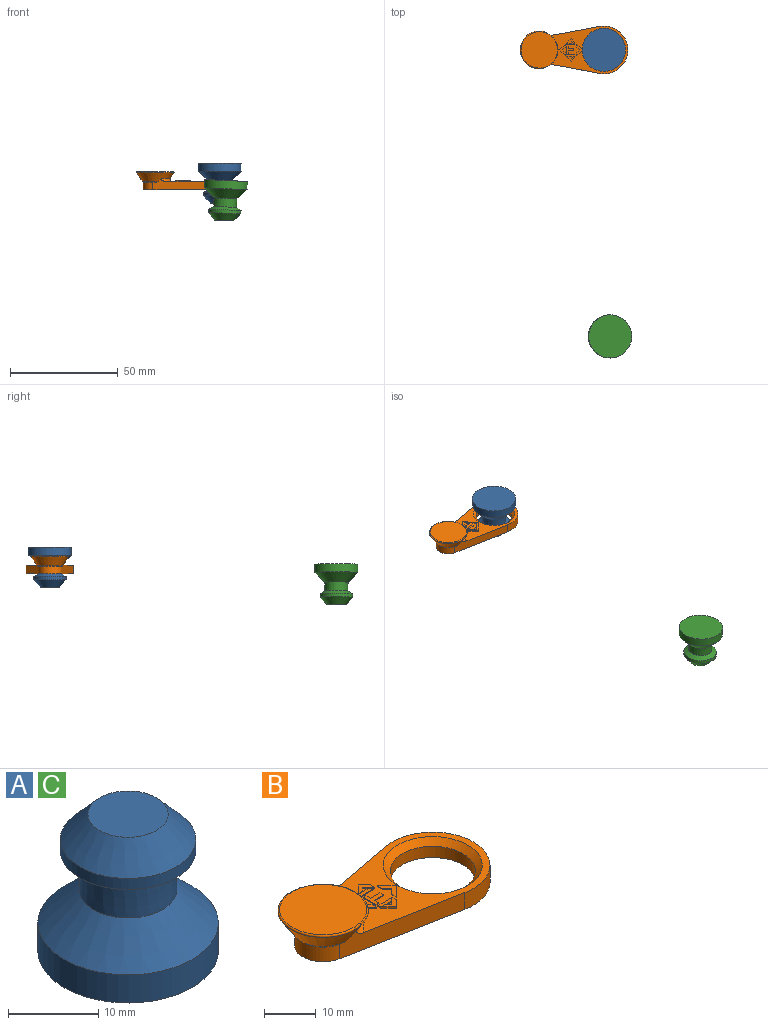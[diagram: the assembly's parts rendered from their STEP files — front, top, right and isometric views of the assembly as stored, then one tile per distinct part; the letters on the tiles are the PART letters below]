
ASSEMBLY  parts=3 mates=1
PART A: 8 faces, bbox 20x20x18.6 mm
  f0: cylinder r=7.51mm len=15.03mm, axis (0,0,1), area 71.2mm2, adj f1,f7
  f1: cone r=7.51mm half-angle=57.5deg, axis (0,0,1), area 104.1mm2, adj f0,f2
  f2: cone r=5.34mm half-angle=0.8deg, axis (0,0,-1), area 133.8mm2, adj f1,f3
  f3: cone r=10mm half-angle=45.9deg, axis (0,0,-1), area 310.4mm2, adj f2,f4
  f4: cylinder r=10mm len=20mm, axis (0,0,1), area 239.6mm2, adj f3,f5
  f5: plane 20x20mm, normal (0,0,-1), area 314.2mm2, adj f4
  f6: plane 8.89x8.89mm, normal (0,0,1), area 62.1mm2, adj f7
  f7: cone r=4.45mm half-angle=41.9deg, axis (0,0,-1), area 172.6mm2, adj f0,f6
PART B: 64 faces, bbox 50.6x22.2x8.5 mm
  f0: plane 36.62x22.2mm, normal (0,0,1), area 296.5mm2, adj f3,f8,f9,f10,f16,f20,f21,f23
  f1: plane 1.72x0.86mm, normal (0,0,1), area 0.7mm2, adj f32,f51,f55
  f2: plane 1.72x0.86mm, normal (0,0,1), area 0.7mm2, adj f19,f45,f46
  f3: cone r=7.6mm half-angle=45deg, axis (0,0,1), area 107.1mm2, adj f0,f18
  f4: plane 16.88x16.88mm, normal (0,0,1), area 223.8mm2, adj f17
  f5: cone r=6mm half-angle=33.7deg, axis (0,0,1), area 197.3mm2, adj f8,f9,f13,f14,f15,f16,f17
  f6: cylinder r=5.53mm len=10.86mm, axis (0,0,-1), area 53.5mm2, adj f8,f9,f11,f14
  f7: cylinder r=4.03mm len=8.05mm, axis (0,0,-1), area 199.8mm2, adj f11,f12
  f8: plane 28.96x5.55mm, normal (-0.19,0.98,0), area 118.4mm2, adj f0,f5,f6,f10,f11,f13,f16
  f9: plane 28.96x5.55mm, normal (-0.19,-0.98,0), area 118.4mm2, adj f0,f5,f6,f10,f11,f15,f16
  f10: cylinder r=11.1mm len=22.2mm, axis (0,0,-1), area 156.1mm2, adj f0,f8,f9,f11
  f11: plane 46.63x22.2mm, normal (0,0,-1), area 484.2mm2, adj f6,f7,f8,f9,f10,f18
  f12: plane 8.05x8.05mm, normal (0,0,-1), area 50.9mm2, adj f7
  f13: plane 1.32x0.45mm, normal (-0.13,0.69,-0.71), area 0.5mm2, adj f5,f8,f14
  f14: cone r=5.53mm half-angle=45deg, axis (0,0,1), area 9.5mm2, adj f5,f6,f13,f15
  f15: plane 1.32x0.45mm, normal (-0.13,-0.69,-0.71), area 0.5mm2, adj f5,f9,f14
  f16: torus R=7.87mm, axis (0,0,1), area 33.1mm2, adj f0,f5,f8,f9
  f17: torus R=8.44mm, axis (0,0,1), area 35.2mm2, adj f4,f5
  f18: cylinder r=8.25mm len=16.5mm, axis (0,0,-1), area 137.4mm2, adj f3,f11
  f19: plane 1.72x0.2mm, normal (0,1,0), area 0.3mm2, adj f2,f22,f45,f46
  f20: plane 0.8x0.2mm, normal (-1,0,0), area 0.2mm2, adj f0,f21,f22,f44
  f21: plane 3.79x0.2mm, normal (0,-1,0), area 0.8mm2, adj f0,f20,f22,f47
  f22: plane 3.79x0.8mm, normal (0,0,1), area 2.7mm2, adj f19,f20,f21,f43,f46
  f23: plane 3.51x0.2mm, normal (-1,0,0), area 0.7mm2, adj f0,f24,f30,f31
  f24: plane 0.8x0.2mm, normal (0,-1,0), area 0.2mm2, adj f0,f23,f25,f31
  f25: plane 1.28x0.2mm, normal (1,0,0), area 0.3mm2, adj f0,f24,f26,f31
  f26: plane 2.53x0.2mm, normal (0,-1,0), area 0.5mm2, adj f0,f25,f27,f31
  f27: plane 0.94x0.2mm, normal (1,0,0), area 0.2mm2, adj f0,f26,f28,f31
  f28: plane 2.53x0.2mm, normal (0,1,0), area 0.5mm2, adj f0,f27,f29,f31
  f29: plane 1.28x0.2mm, normal (1,0,0), area 0.3mm2, adj f0,f28,f30,f31
  f30: plane 0.8x0.2mm, normal (0,1,0), area 0.2mm2, adj f0,f23,f29,f31
  f31: plane 3.51x3.33mm, normal (0,0,1), area 5.2mm2, adj f23,f24,f25,f26,f27,f28,f29,f30
  f32: plane 1.72x0.2mm, normal (0,-1,0), area 0.3mm2, adj f1,f35,f51,f55
  f33: plane 3.79x0.2mm, normal (0,1,0), area 0.8mm2, adj f0,f34,f35,f54
  f34: plane 0.8x0.2mm, normal (-1,0,0), area 0.2mm2, adj f0,f33,f35,f52
  f35: plane 3.79x0.8mm, normal (0,0,1), area 2.7mm2, adj f32,f33,f34,f50,f51
  f36: plane 2.56x2.56mm, normal (-0.71,0.71,0), area 1.1mm2, adj f0,f37,f41,f42
  f37: plane 2.56x2.56mm, normal (-0.71,-0.71,0), area 1.1mm2, adj f0,f36,f38,f42
  f38: plane 1.27x0.3mm, normal (1,0,0), area 0.4mm2, adj f0,f37,f39,f42
  f39: plane 1.28x1.28mm, normal (0.71,0.71,0), area 0.5mm2, adj f0,f38,f40,f42
  f40: plane 1.28x1.28mm, normal (0.71,-0.71,0), area 0.5mm2, adj f0,f39,f41,f42
  f41: plane 1.27x0.3mm, normal (1,0,0), area 0.4mm2, adj f0,f36,f40,f42
  f42: plane 5.11x2.56mm, normal (0,0,1), area 4.9mm2, adj f36,f37,f38,f39,f40,f41
  f43: plane 1.27x0.1mm, normal (0,-1,0), area 0.1mm2, adj f22,f44,f45,f49
  f44: plane 2.13x2.13mm, normal (-0.71,0.71,0), area 0.9mm2, adj f0,f20,f43,f48,f49
  f45: plane 0.86x0.86mm, normal (0.71,-0.71,0), area 0.4mm2, adj f2,f19,f43,f46,f49
  f46: plane 1.66x1.66mm, normal (-0.71,-0.71,0), area 0.5mm2, adj f2,f19,f22,f45,f47,f49
  f47: plane 1.27x0.3mm, normal (1,0,0), area 0.4mm2, adj f0,f21,f46,f48,f49
  f48: plane 1.66x1.66mm, normal (0.71,0.71,0), area 0.7mm2, adj f0,f44,f47,f49
  f49: plane 3.79x2.93mm, normal (0,0,1), area 4mm2, adj f43,f44,f45,f46,f47,f48
  f50: plane 1.27x0.1mm, normal (0,1,0), area 0.1mm2, adj f35,f52,f55,f56
  f51: plane 1.66x1.66mm, normal (-0.71,0.71,0), area 0.5mm2, adj f1,f32,f35,f54,f55,f56
  f52: plane 2.13x2.13mm, normal (-0.71,-0.71,0), area 0.9mm2, adj f0,f34,f50,f53,f56
  f53: plane 1.66x1.66mm, normal (0.71,-0.71,0), area 0.7mm2, adj f0,f52,f54,f56
  f54: plane 1.27x0.3mm, normal (1,0,0), area 0.4mm2, adj f0,f33,f51,f53,f56
  f55: plane 0.86x0.86mm, normal (0.71,0.71,0), area 0.4mm2, adj f1,f32,f50,f51,f56
  f56: plane 3.79x2.93mm, normal (0,0,1), area 4mm2, adj f50,f51,f52,f53,f54,f55
  f57: plane 2.56x2.56mm, normal (0.71,0.71,0), area 0.4mm2, adj f0,f58,f62,f63
  f58: plane 1.27x0.1mm, normal (-1,0,0), area 0.1mm2, adj f0,f57,f59,f63
  f59: plane 1.28x1.28mm, normal (-0.71,-0.71,0), area 0.2mm2, adj f0,f58,f60,f63
  f60: plane 1.28x1.28mm, normal (-0.71,0.71,0), area 0.2mm2, adj f0,f59,f61,f63
  f61: plane 1.27x0.1mm, normal (-1,0,0), area 0.1mm2, adj f0,f60,f62,f63
  f62: plane 2.56x2.56mm, normal (0.71,-0.71,0), area 0.4mm2, adj f0,f57,f61,f63
  f63: plane 5.11x2.56mm, normal (0,0,1), area 4.9mm2, adj f57,f58,f59,f60,f61,f62
PART C: same geometry as A
PLACE A rot(axis=(0,-1,0),180deg) t=(3.97,18.86,50.62)mm
PLACE B t=(4.55,18.86,38.14)mm
PLACE C rot(axis=(0,-1,0),177.5deg) t=(6.87,-113.98,42.57)mm
MATE slider A.f0 <-> B.f3  axis (0,0,1) through (4.55,18.86,44.57)mm
